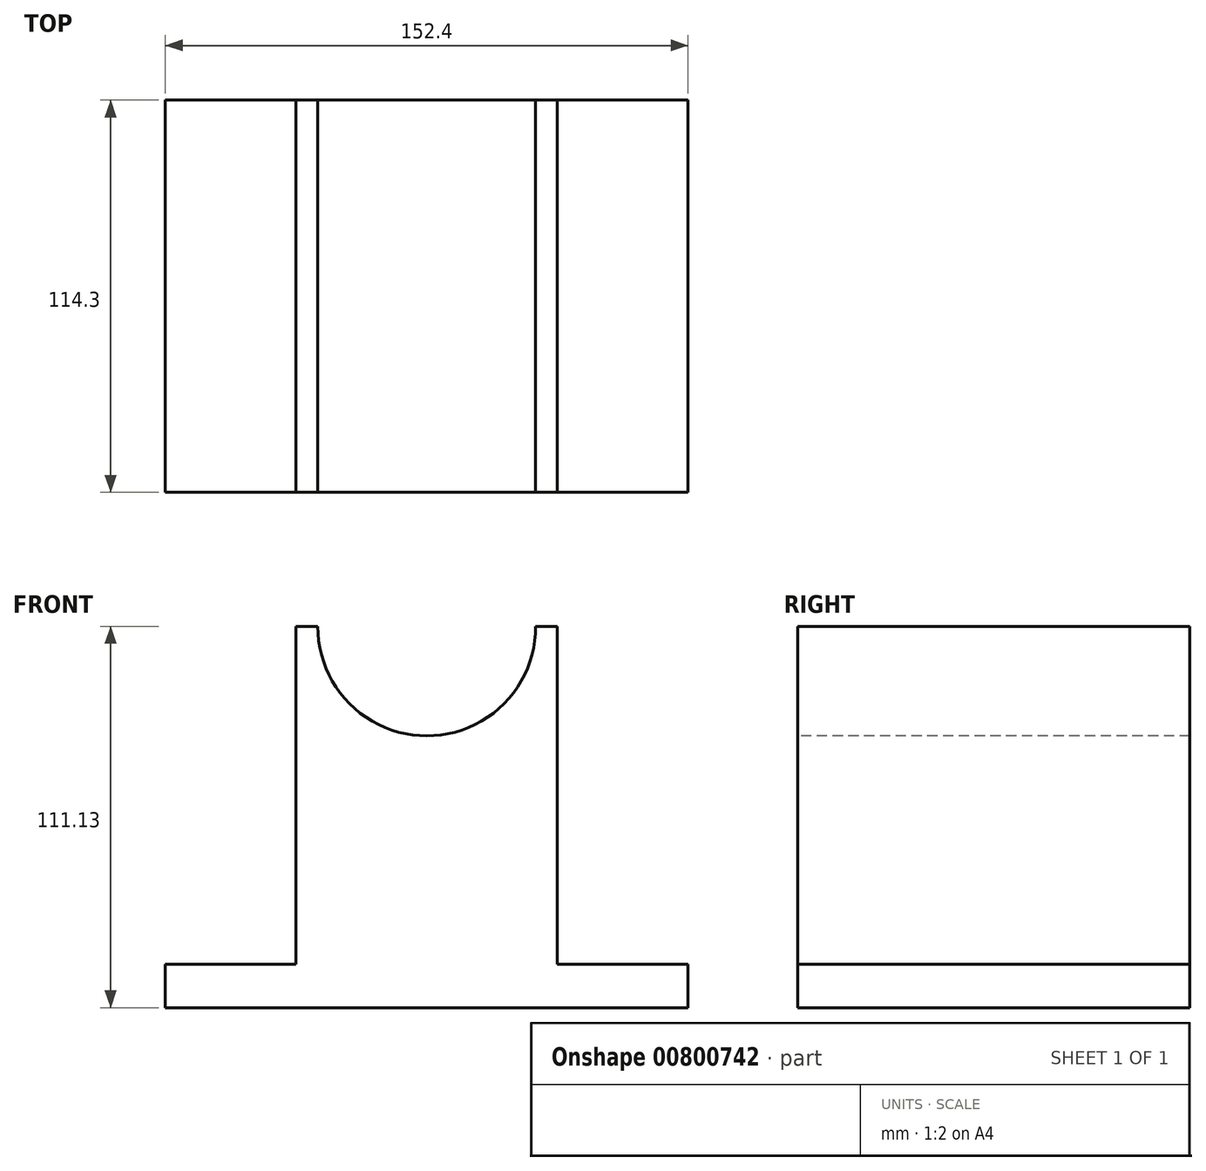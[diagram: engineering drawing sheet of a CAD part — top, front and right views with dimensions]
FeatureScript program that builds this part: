
annotation { "Feature Type Name" : "Feature", "Feature Type Description" : "" }
export const myFeature = defineFeature(function(context is Context, id is Id, definition is map)
    precondition{}
    {
        {
            var Q0;
            Q0=qCreatedBy(makeId("Front.planeOp"),FACE);
            var sketch = newSketch(context, id + "F0", { "sketchPlane" : qUnion([Q0])});
            skLineSegment(sketch, "E0", {"start": v(0, 0) * mm, "end": v(38.1, 0) * mm});
            skLineSegment(sketch, "E1", {"start": v(38.1, 0) * mm, "end": v(38.1, 98.43) * mm});
            skLineSegment(sketch, "E2", {"start": v(38.1, 98.43) * mm, "end": v(114.3, 98.43) * mm});
            skLineSegment(sketch, "E3", {"start": v(114.3, 98.43) * mm, "end": v(114.3, 0) * mm});
            skLineSegment(sketch, "E4", {"start": v(114.3, 0) * mm, "end": v(152.4, 0) * mm});
            skLineSegment(sketch, "E5", {"start": v(152.4, 0) * mm, "end": v(152.4, -12.7) * mm});
            skLineSegment(sketch, "E6", {"start": v(152.4, -12.7) * mm, "end": v(0, -12.7) * mm});
            skLineSegment(sketch, "E7", {"start": v(0, 0) * mm, "end": v(0, -12.7) * mm});
            skSolve(sketch);
        }
        {
            var Q0;
            Q0=makeQuery(id+"F0.imprint","IMPRINT",FACE,{"disambiguationData":[TD([[makeQuery(id+"F0.imprint","IMPRINT",EDGE,{"derivedFrom":sQuery(id+"F0.wireOp",EDGE,"E0")}),-1.0]])]});
            extrude(context, id + "F1", {"entities" : qUnion([Q0]), "depth" : 114.3 * mm, "offsetDistance" : 25.4 * mm});
        }
        {
            var Q0;
            Q0=makeQuery(id+"F1.opExtrude","CAP_FACE",FACE,{"disambiguationData":[OSD([sQuery(id+"F0.wireOp",EDGE,"E0"),sQuery(id+"F0.wireOp",EDGE,"E1"),sQuery(id+"F0.wireOp",EDGE,"E2"),sQuery(id+"F0.wireOp",EDGE,"E3"),sQuery(id+"F0.wireOp",EDGE,"E4"),sQuery(id+"F0.wireOp",EDGE,"E5"),sQuery(id+"F0.wireOp",EDGE,"E6"),sQuery(id+"F0.wireOp",EDGE,"E7")])],"isStart":false});
            var sketch = newSketch(context, id + "F2", { "sketchPlane" : qUnion([Q0])});
            skLineSegment(sketch, "E8", {"start": v(38.1, 98.43) * mm, "end": v(44.45, 98.43) * mm});
            skLineSegment(sketch, "E9", {"start": v(114.3, 98.43) * mm, "end": v(107.95, 98.43) * mm});
            skArc(sketch, "E10", {"start": v(44.45, 98.43) * mm, "mid": v(76.2, 89.92) * mm, "end": v(107.95, 98.42) * mm});
            skSolve(sketch);
        }
        {
            var Q0;
            {var subQ0=sQuery(id+"F2.wireOp",EDGE,"E10");Q0=makeQuery(id+"F2.imprint","IMPRINT",FACE,{"disambiguationData":[TD([[makeQuery(id+"F2.imprint","IMPRINT",EDGE,{"derivedFrom":subQ0}),1.0]])]});}
            extrude(context, id + "F3", {"entities" : qUnion([Q0]), "operationType" : NewBodyOperationType.REMOVE, "oppositeDirection" : true, "depth" : 114.3 * mm, "offsetDistance" : 25.4 * mm});
        }
        {
            var Q0;
            Q0=makeQuery(id+"F1.opExtrude","CAP_FACE",FACE,{"disambiguationData":[OSD([sQuery(id+"F0.wireOp",EDGE,"E0"),sQuery(id+"F0.wireOp",EDGE,"E1"),sQuery(id+"F0.wireOp",EDGE,"E2"),sQuery(id+"F0.wireOp",EDGE,"E3"),sQuery(id+"F0.wireOp",EDGE,"E4"),sQuery(id+"F0.wireOp",EDGE,"E5"),sQuery(id+"F0.wireOp",EDGE,"E6"),sQuery(id+"F0.wireOp",EDGE,"E7")])],"isStart":false});
            var sketch = newSketch(context, id + "F4", { "sketchPlane" : qUnion([Q0])});
            skArc(sketch, "E11", {"start": v(44.45, 98.42) * mm, "mid": v(76.2, 66.5) * mm, "end": v(107.95, 98.42) * mm});
            skSolve(sketch);
        }
        {
            var Q0;
            Q0=makeQuery(id+"F4.imprint","IMPRINT",FACE,{"disambiguationData":[TD([[makeQuery(id+"F4.imprint","IMPRINT",EDGE,{"derivedFrom":sQuery(id+"F4.wireOp",EDGE,"E11")}),1.0]])]});
            extrude(context, id + "F5", {"entities" : qUnion([Q0]), "operationType" : NewBodyOperationType.REMOVE, "endBound" : BoundingType.THROUGH_ALL, "oppositeDirection" : true, "depth" : 25.4 * mm, "offsetDistance" : 25.4 * mm});
        }
    });
